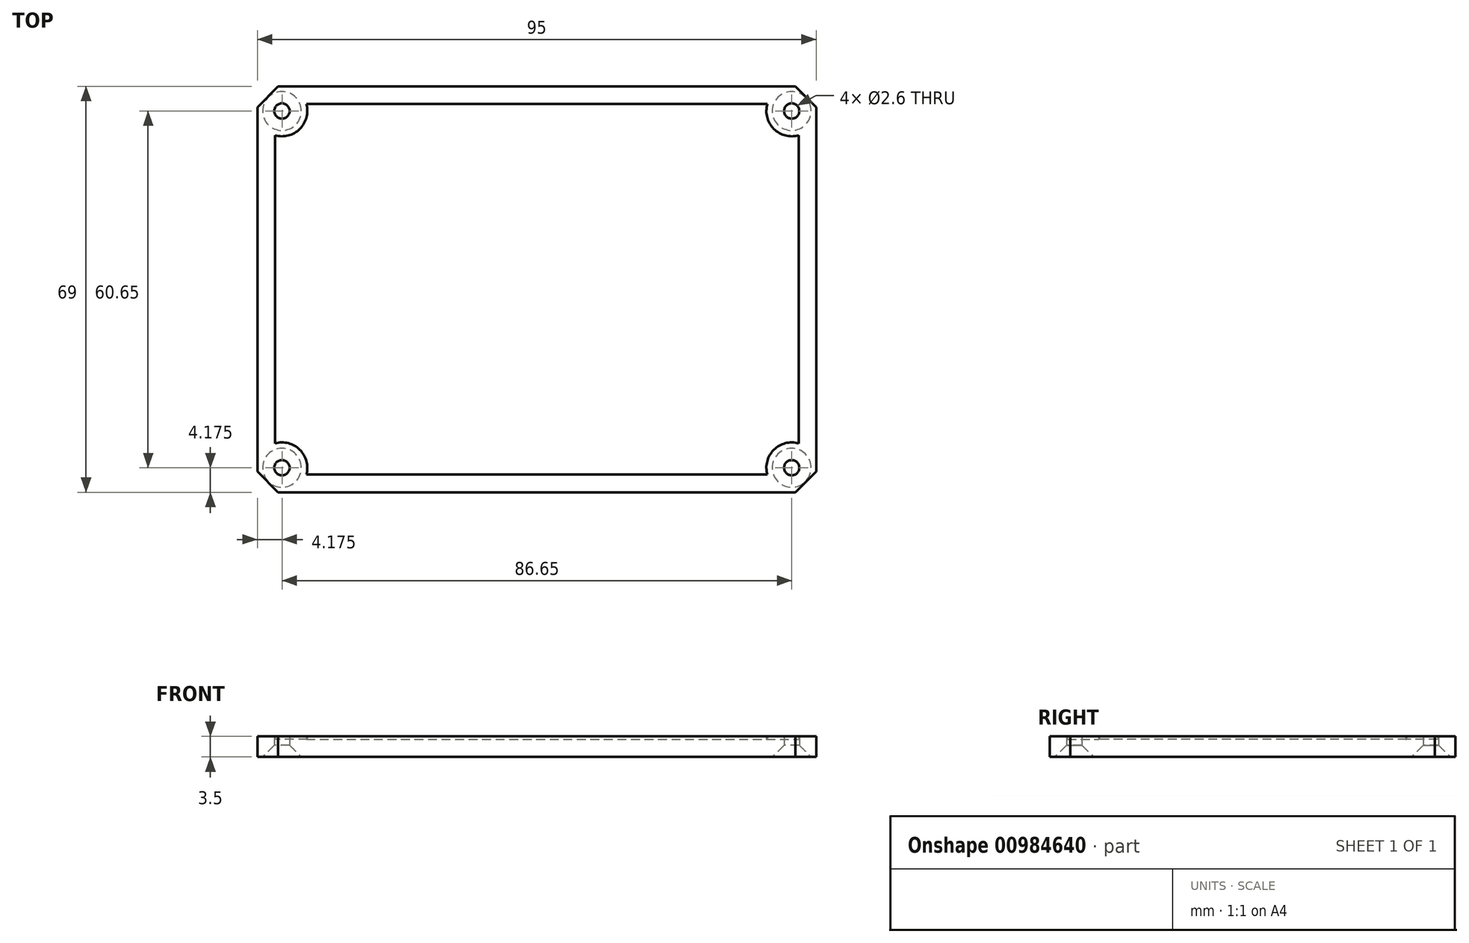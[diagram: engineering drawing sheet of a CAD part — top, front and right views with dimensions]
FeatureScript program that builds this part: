
annotation { "Feature Type Name" : "Feature", "Feature Type Description" : "" }
export const myFeature = defineFeature(function(context is Context, id is Id, definition is map)
    precondition{}
    {
        {
            var Q0;
            Q0=qCreatedBy(makeId("Top.planeOp"),FACE);
            var sketch = newSketch(context, id + "F0", { "sketchPlane" : qUnion([Q0])});
            skLineSegment(sketch, "E0", {"start": v(0, 60.57) * mm, "end": v(0, -52.9) * mm, "construction": true});
            skLineSegment(sketch, "E1", {"start": v(-43.96, 34.5) * mm, "end": v(-39.15, 34.5) * mm});
            skLineSegment(sketch, "E2", {"start": v(47.5, 30.96) * mm, "end": v(47.5, 0) * mm});
            skLineSegment(sketch, "E3", {"start": v(-47.5, 30.96) * mm, "end": v(-47.5, 0) * mm});
            skLineSegment(sketch, "E4.MirrorCS", {"start": v(-43.96, -34.5) * mm, "end": v(-39.15, -34.5) * mm});
            skLineSegment(sketch, "E5.MirrorCS", {"start": v(-47.5, -30.96) * mm, "end": v(-47.5, 0) * mm});
            skLineSegment(sketch, "E6.MirrorCS", {"start": v(47.5, -30.96) * mm, "end": v(47.5, 0) * mm});
            skLineSegment(sketch, "E7", {"start": v(-47.5, 30.96) * mm, "end": v(-43.96, 34.5) * mm});
            skLineSegment(sketch, "E8.MirrorCS", {"start": v(47.5, 30.96) * mm, "end": v(43.96, 34.5) * mm});
            skLineSegment(sketch, "E9.MirrorCS", {"start": v(-47.5, -30.96) * mm, "end": v(-43.96, -34.5) * mm});
            skLineSegment(sketch, "E10.MirrorCS", {"start": v(47.5, -30.96) * mm, "end": v(43.96, -34.5) * mm});
            skPoint(sketch, "E11.orphan", {"position": v(-47.5, 34.5) * mm});
            skPoint(sketch, "E12.orphan", {"position": v(-47.5, -34.5) * mm});
            skPoint(sketch, "E13.orphan", {"position": v(47.5, -34.5) * mm});
            skPoint(sketch, "E14.orphan", {"position": v(47.5, 34.5) * mm});
            skLineSegment(sketch, "E15", {"start": v(-27.15, 59.52) * mm, "end": v(-27.15, -44.22) * mm, "construction": true});
            skLineSegment(sketch, "E16", {"start": v(-27.15, 34.5) * mm, "end": v(-27.15, 32.7) * mm});
            skLineSegment(sketch, "E17.MirrorCS", {"start": v(39.15, 34.5) * mm, "end": v(39.15, 34.5) * mm});
            skLineSegment(sketch, "E18.MirrorCS", {"start": v(-39.15, -32.7) * mm, "end": v(-39.15, -34.5) * mm});
            skLineSegment(sketch, "E19.MirrorCS", {"start": v(39.15, -32.7) * mm, "end": v(39.15, -34.5) * mm});
            skLineSegment(sketch, "E20.trimOffspring", {"start": v(-27.15, 34.5) * mm, "end": v(27.15, 34.5) * mm});
            skLineSegment(sketch, "E21.trimOffspring", {"start": v(39.15, 34.5) * mm, "end": v(43.96, 34.5) * mm});
            skLineSegment(sketch, "E22.trimOffspring", {"start": v(39.15, -34.5) * mm, "end": v(43.96, -34.5) * mm});
            skLineSegment(sketch, "E23.trimOffspring", {"start": v(-27.15, -34.5) * mm, "end": v(27.15, -34.5) * mm});
            skLineSegment(sketch, "E24", {"start": v(-39.15, 34.5) * mm, "end": v(-27.15, 34.5) * mm});
            skLineSegment(sketch, "E25", {"start": v(27.15, 34.5) * mm, "end": v(39.15, 34.5) * mm});
            skLineSegment(sketch, "E26", {"start": v(27.15, -34.5) * mm, "end": v(39.15, -34.5) * mm});
            skLineSegment(sketch, "E27", {"start": v(-39.15, -34.5) * mm, "end": v(-27.15, -34.5) * mm});
            skLineSegment(sketch, "E28", {"start": v(-39.15, 34.5) * mm, "end": v(-39.15, 26.15) * mm});
            skLineSegment(sketch, "E29", {"start": v(-39.15, 26.15) * mm, "end": v(-47.5, 26.15) * mm});
            skLineSegment(sketch, "E30", {"start": v(-48.88, 30.32) * mm, "end": v(-34.6, 30.32) * mm, "construction": true});
            skLineSegment(sketch, "E31", {"start": v(-43.33, 24.98) * mm, "end": v(-43.33, 37.43) * mm, "construction": true});
            skCircle(sketch, "E32", {"center": v(-43.33, 30.32) * mm, "radius": 1.3 * mm});
            skLineSegment(sketch, "E33.MirrorCS", {"start": v(43.96, 34.5) * mm, "end": v(39.15, 34.5) * mm});
            skLineSegment(sketch, "E34.MirrorCS", {"start": v(43.33, 24.98) * mm, "end": v(43.33, 37.43) * mm, "construction": true});
            skCircle(sketch, "E35.MirrorC", {"center": v(43.33, 30.32) * mm, "radius": 1.3 * mm});
            skLineSegment(sketch, "E36.MirrorCS", {"start": v(39.15, 26.15) * mm, "end": v(47.5, 26.15) * mm});
            skLineSegment(sketch, "E37.MirrorCS", {"start": v(48.88, 30.32) * mm, "end": v(34.6, 30.32) * mm, "construction": true});
            skLineSegment(sketch, "E38.MirrorCS", {"start": v(39.15, 34.5) * mm, "end": v(39.15, 26.15) * mm});
            skLineSegment(sketch, "E39.MirrorCS", {"start": v(-39.15, -26.15) * mm, "end": v(-47.5, -26.15) * mm});
            skLineSegment(sketch, "E40.MirrorCS", {"start": v(-43.33, -24.98) * mm, "end": v(-43.33, -37.43) * mm, "construction": true});
            skLineSegment(sketch, "E41.MirrorCS", {"start": v(-39.15, -32.7) * mm, "end": v(-39.15, -26.15) * mm});
            skCircle(sketch, "E42.MirrorC", {"center": v(-43.33, -30.32) * mm, "radius": 1.3 * mm});
            skLineSegment(sketch, "E43.MirrorCS", {"start": v(-48.88, -30.32) * mm, "end": v(-34.6, -30.32) * mm, "construction": true});
            skLineSegment(sketch, "E44.MirrorCS", {"start": v(43.96, -34.5) * mm, "end": v(39.15, -34.5) * mm});
            skCircle(sketch, "E45.MirrorC", {"center": v(43.33, -30.32) * mm, "radius": 1.3 * mm});
            skLineSegment(sketch, "E46.MirrorCS", {"start": v(48.88, -30.32) * mm, "end": v(34.6, -30.32) * mm, "construction": true});
            skLineSegment(sketch, "E47.MirrorCS", {"start": v(43.33, -24.98) * mm, "end": v(43.33, -37.43) * mm, "construction": true});
            skLineSegment(sketch, "E48.MirrorCS", {"start": v(39.15, -32.7) * mm, "end": v(39.15, -26.15) * mm});
            skLineSegment(sketch, "E49.MirrorCS", {"start": v(39.15, -26.15) * mm, "end": v(47.5, -26.15) * mm});
            skLineSegment(sketch, "E50", {"start": v(-47.5, 30.96) * mm, "end": v(-47.5, 26.15) * mm});
            skLineSegment(sketch, "E51", {"start": v(47.5, 30.96) * mm, "end": v(47.5, 26.15) * mm});
            skLineSegment(sketch, "E52", {"start": v(-47.5, -30.96) * mm, "end": v(-47.5, -26.15) * mm});
            skLineSegment(sketch, "E53", {"start": v(47.5, -26.15) * mm, "end": v(47.5, -30.96) * mm});
            skSolve(sketch);
        }
        {
            var Q0;
            Q0 = qSketchRegion(id + "F0", true);
            extrude(context, id + "F1", {"entities" : qUnion([Q0]), "depth" : 3.5 * mm, "offsetDistance" : 25 * mm});
        }
        {
            var Q0;
            Q0=makeQuery(id+"F1.opExtrude","CAP_FACE",FACE,{"disambiguationData":[OSD([sQuery(id+"F0.wireOp",EDGE,"E1"),sQuery(id+"F0.wireOp",EDGE,"E2"),sQuery(id+"F0.wireOp",EDGE,"E3"),sQuery(id+"F0.wireOp",EDGE,"E7"),sQuery(id+"F0.wireOp",EDGE,"E20.trimOffspring"),sQuery(id+"F0.wireOp",EDGE,"E23.trimOffspring"),sQuery(id+"F0.wireOp",EDGE,"E24"),sQuery(id+"F0.wireOp",EDGE,"E25"),sQuery(id+"F0.wireOp",EDGE,"E32"),sQuery(id+"F0.wireOp",EDGE,"E33.MirrorCS"),sQuery(id+"F0.wireOp",EDGE,"E35.MirrorC"),sQuery(id+"F0.wireOp",EDGE,"E8.MirrorCS"),sQuery(id+"F0.wireOp",EDGE,"E5.MirrorCS"),sQuery(id+"F0.wireOp",EDGE,"E4.MirrorCS"),sQuery(id+"F0.wireOp",EDGE,"E27"),sQuery(id+"F0.wireOp",EDGE,"E42.MirrorC"),sQuery(id+"F0.wireOp",EDGE,"E9.MirrorCS"),sQuery(id+"F0.wireOp",EDGE,"E22.trimOffspring"),sQuery(id+"F0.wireOp",EDGE,"E26"),sQuery(id+"F0.wireOp",EDGE,"E10.MirrorCS"),sQuery(id+"F0.wireOp",EDGE,"E45.MirrorC"),sQuery(id+"F0.wireOp",EDGE,"E6.MirrorCS"),sQuery(id+"F0.wireOp",EDGE,"E51"),sQuery(id+"F0.wireOp",EDGE,"E50"),sQuery(id+"F0.wireOp",EDGE,"E52"),sQuery(id+"F0.wireOp",EDGE,"E53")])],"isStart":false});
            shell(context, id + "F2", {"entities" : qUnion([Q0]), "thickness" : 3 * mm});
        }
        {
            var Q0;
            Q0=makeQuery(id+"F1.opExtrude","CAP_EDGE",EDGE,{"disambiguationData":[OSD([sQuery(id+"F0.wireOp",EDGE,"E35.MirrorC")])],"isStart":true});
            var Q1;
            Q1=makeQuery(id+"F1.opExtrude","CAP_EDGE",EDGE,{"disambiguationData":[OSD([sQuery(id+"F0.wireOp",EDGE,"E45.MirrorC")])],"isStart":true});
            var Q2;
            Q2=makeQuery(id+"F1.opExtrude","CAP_EDGE",EDGE,{"disambiguationData":[OSD([sQuery(id+"F0.wireOp",EDGE,"E42.MirrorC")])],"isStart":true});
            var Q3;
            Q3=makeQuery(id+"F1.opExtrude","CAP_EDGE",EDGE,{"disambiguationData":[OSD([sQuery(id+"F0.wireOp",EDGE,"E32")])],"isStart":true});
            chamfer(context, id + "F3", {"entities" : qUnion([Q0, Q1, Q2, Q3]), "width" : 2 * mm, "tangentPropagation" : true});
        }
    });
